# Revit family: Artek_Shelving_Kaari Wall Shelf with Desk_Kaari REB010
name_source: partatom
category: Furniture
revit_build: Autodesk Revit 2017 (Build: 20190508_0315(x64)
units: mm (PartAtom-declared; Revit-internal decimal feet)

## family parameters
Cut with Voids When Loaded = No
Host = Face
OmniClass Number = 23.40.20.27
OmniClass Title = Storage Shelving
Room Calculation Point = No
Shared = No

## types (1)
- Kaari shelf with desk REB010
    AssetType = Movable
    BIMObjectName = Artek_Shelving_Kaari Wall Shelf with Desk_Kaari REB010
    Brand = Artek
    Category = Shelving
    Collection = Kaari Collection
    Color = Black
    ConvergoRefNr = 0190-2009-0037-FI
    Default Elevation = 0 mm  [stored 0 ft]
    Designer = Ronan & Erwan Bouroullec
    DurationUnit = Years
    IfcExportAs = IfcFurnitureType
    IfcExportType = SHELF
    LegsMaterial = Solid oak
    MainColor = Black
    Manufacturer = Artek
    ManufacturerName = Artek
    ManufacturerURL = https://www.artek.fi
    Material = Wood/Steel
    Model = Kaari REB010
    ModelNumber = 28503001
    NBSDescription = Shelf units
    NBSReference = 45-35-80/310
    Name = Kaari REB010
    NominalDepth = 1416 mm
    NominalHeight = 2000 mm  [stored 6.56168 ft]
    NominalWidth = 550 mm
    Shape = Sculptured
    ShelfTopMaterial = Melamine
    Size = 2000x1420x550 mm
    URL = https://www.artek.fi
    Uniclass2 = Pr_40_30_78_77
    Uniclass2015Description = Shelf units
    Uniclass2015Reference = Pr_40_30_78_77
    Version = 1
    VersionDate = 11/3/2020
    WarrantyDurationUnit = Years

note: [stored X ft] marks values corroborated as IEEE doubles in the binary element streams (Revit-internal decimal feet)

## geometry (parser evidence)
native form markers: Sweep x4
no freeform markers — native parametric forms only
